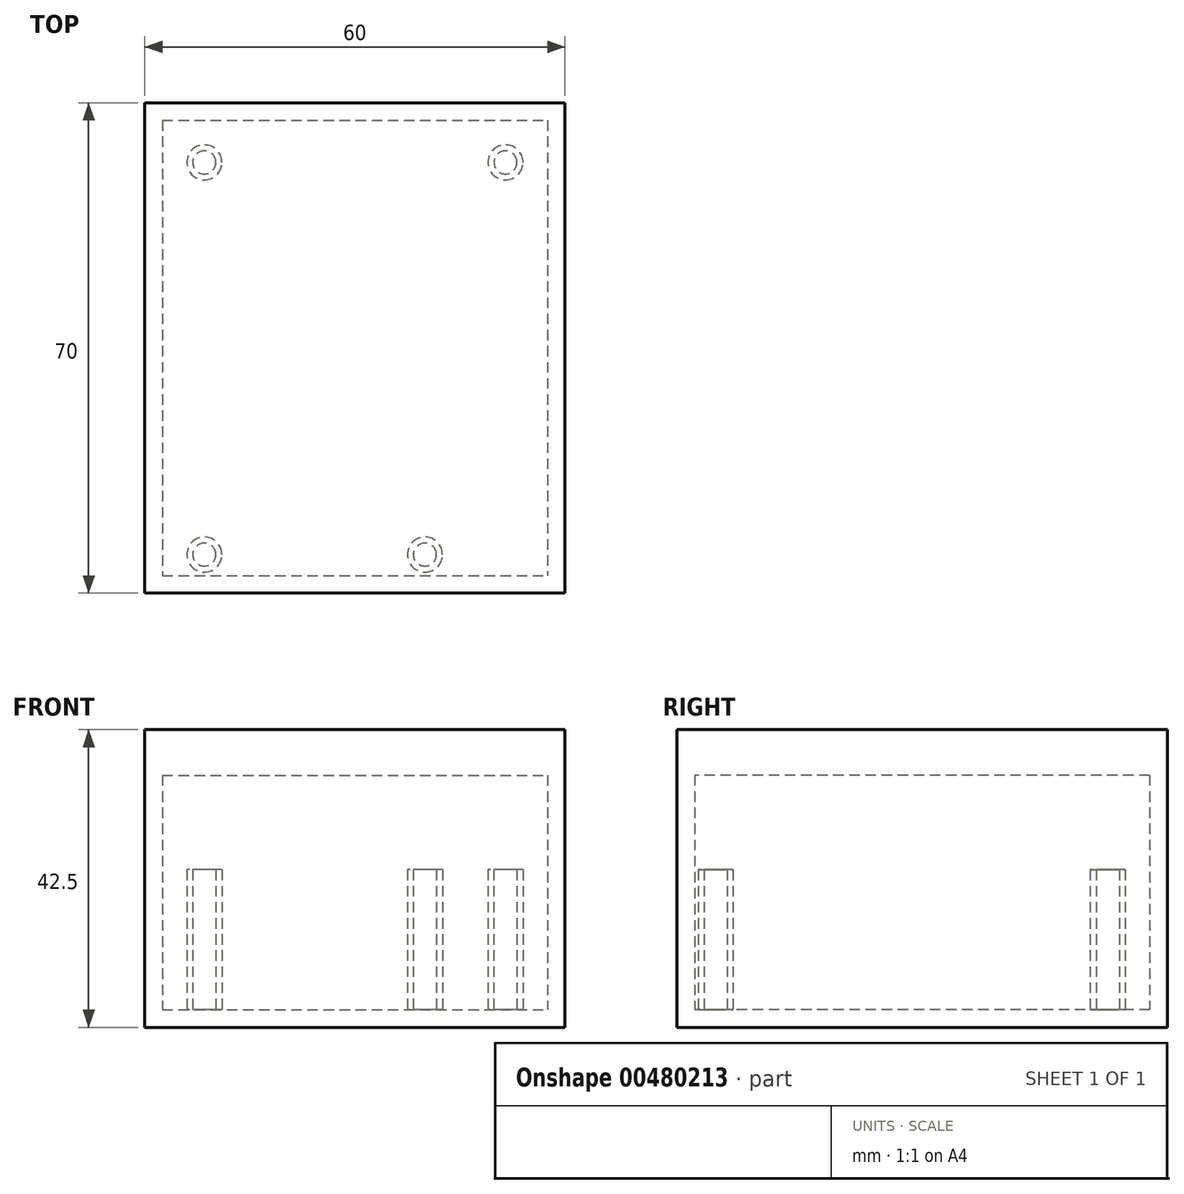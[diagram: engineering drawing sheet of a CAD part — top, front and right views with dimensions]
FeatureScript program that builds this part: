
annotation { "Feature Type Name" : "Feature", "Feature Type Description" : "" }
export const myFeature = defineFeature(function(context is Context, id is Id, definition is map)
    precondition{}
    {
        {
            var Q0;
            Q0=qCreatedBy(makeId("Top.planeOp"),FACE);
            var sketch = newSketch(context, id + "F0", { "sketchPlane" : qUnion([Q0])});
            skLineSegment(sketch, "E0.bottom", {"start": v(-30, 35) * mm, "end": v(30, 35) * mm});
            skLineSegment(sketch, "E0.top", {"start": v(-30, -35) * mm, "end": v(30, -35) * mm});
            skLineSegment(sketch, "E0.left", {"start": v(-30, 35) * mm, "end": v(-30, -35) * mm});
            skLineSegment(sketch, "E0.right", {"start": v(30, 35) * mm, "end": v(30, -35) * mm});
            skPoint(sketch, "E0.middle", {"position": v(0, 0) * mm});
            skSolve(sketch);
        }
        {
            var Q0;
            Q0 = qSketchRegion(id + "F0", true);
            extrude(context, id + "F1", {"entities" : qUnion([Q0]), "depth" : 40 * mm});
        }
        {
            var Q0;
            Q0=makeQuery(id+"F1.opExtrude","CAP_FACE",FACE,{"disambiguationData":[OSD([sQuery(id+"F0.wireOp",EDGE,"E0.bottom"),sQuery(id+"F0.wireOp",EDGE,"E0.top"),sQuery(id+"F0.wireOp",EDGE,"E0.left"),sQuery(id+"F0.wireOp",EDGE,"E0.right")])],"isStart":false});
            shell(context, id + "F2", {"entities" : qUnion([Q0]), "thickness" : 2.5 * mm});
        }
        {
            var Q0;
            Q0=makeQuery(id+"F1.opExtrude","CAP_FACE",FACE,{"disambiguationData":[OSD([sQuery(id+"F0.wireOp",EDGE,"E0.bottom"),sQuery(id+"F0.wireOp",EDGE,"E0.top"),sQuery(id+"F0.wireOp",EDGE,"E0.left"),sQuery(id+"F0.wireOp",EDGE,"E0.right")])],"isStart":false});
            var sketch = newSketch(context, id + "F3", { "sketchPlane" : qUnion([Q0])});
            skLineSegment(sketch, "E1.bottom", {"start": v(-27.5, 32.5) * mm, "end": v(27.5, 32.5) * mm});
            skLineSegment(sketch, "E1.top", {"start": v(-27.5, -32.5) * mm, "end": v(27.5, -32.5) * mm});
            skLineSegment(sketch, "E1.left", {"start": v(-27.5, 32.5) * mm, "end": v(-27.5, -32.5) * mm});
            skLineSegment(sketch, "E1.right", {"start": v(27.5, 32.5) * mm, "end": v(27.5, -32.5) * mm});
            skLineSegment(sketch, "E2.bottom", {"start": v(-30, 35) * mm, "end": v(30, 35) * mm});
            skLineSegment(sketch, "E2.top", {"start": v(-30, -35) * mm, "end": v(30, -35) * mm});
            skLineSegment(sketch, "E2.left", {"start": v(-30, 35) * mm, "end": v(-30, -35) * mm});
            skLineSegment(sketch, "E2.right", {"start": v(30, 35) * mm, "end": v(30, -35) * mm});
            skSolve(sketch);
        }
        {
            var Q0;
            Q0=makeQuery(id+"F3.imprint","IMPRINT",FACE,{"disambiguationData":[TD([[makeQuery(id+"F3.imprint","IMPRINT",EDGE,{"derivedFrom":sQuery(id+"F3.wireOp",EDGE,"E1.bottom")}),1.0]])]});
            var Q1;
            Q1=makeQuery(id+"F3.imprint","IMPRINT",FACE,{"disambiguationData":[TD([[makeQuery(id+"F3.imprint","IMPRINT",EDGE,{"derivedFrom":sQuery(id+"F3.wireOp",EDGE,"E1.bottom")}),-1.0]])]});
            extrude(context, id + "F4", {"entities" : qUnion([Q0, Q1]), "depth" : 2.5 * mm});
        }
        {
            var Q0;
            Q0=makeQuery(id+"F3.imprint","IMPRINT",FACE,{"disambiguationData":[TD([[makeQuery(id+"F3.imprint","IMPRINT",EDGE,{"derivedFrom":sQuery(id+"F3.wireOp",EDGE,"E1.bottom")}),-1.0]])]});
            extrude(context, id + "F5", {"entities" : qUnion([Q0]), "operationType" : NewBodyOperationType.ADD, "oppositeDirection" : true, "depth" : 4 * mm});
        }
        {
            var Q0;
            Q0=makeQuery(id+"F2.opShell","OFFSET_FACE",FACE,{"disambiguationData":[OSD([sQuery(id+"F0.wireOp",EDGE,"E0.bottom"),sQuery(id+"F0.wireOp",EDGE,"E0.top"),sQuery(id+"F0.wireOp",EDGE,"E0.left"),sQuery(id+"F0.wireOp",EDGE,"E0.right")])]});
            var sketch = newSketch(context, id + "F6", { "sketchPlane" : qUnion([Q0])});
            skCircle(sketch, "E3", {"center": v(-21.5, 26.5) * mm, "radius": 1.65 * mm});
            skCircle(sketch, "E4.MirrorC", {"center": v(21.5, 26.5) * mm, "radius": 1.65 * mm});
            skCircle(sketch, "E5", {"center": v(-21.5, -29.5) * mm, "radius": 1.65 * mm});
            skCircle(sketch, "E6", {"center": v(10, -29.5) * mm, "radius": 1.65 * mm});
            skCircle(sketch, "E7", {"center": v(-21.5, 26.5) * mm, "radius": 2.5 * mm});
            skCircle(sketch, "E8.MirrorC", {"center": v(21.5, 26.5) * mm, "radius": 2.5 * mm});
            skCircle(sketch, "E9", {"center": v(-21.5, -29.5) * mm, "radius": 2.5 * mm});
            skCircle(sketch, "E10", {"center": v(10, -29.5) * mm, "radius": 2.5 * mm});
            skSolve(sketch);
        }
        {
            var Q0;
            Q0 = qSketchRegion(id + "F6", true);
            extrude(context, id + "F7", {"entities" : qUnion([Q0]), "operationType" : NewBodyOperationType.ADD, "depth" : 20 * mm});
        }
    });
